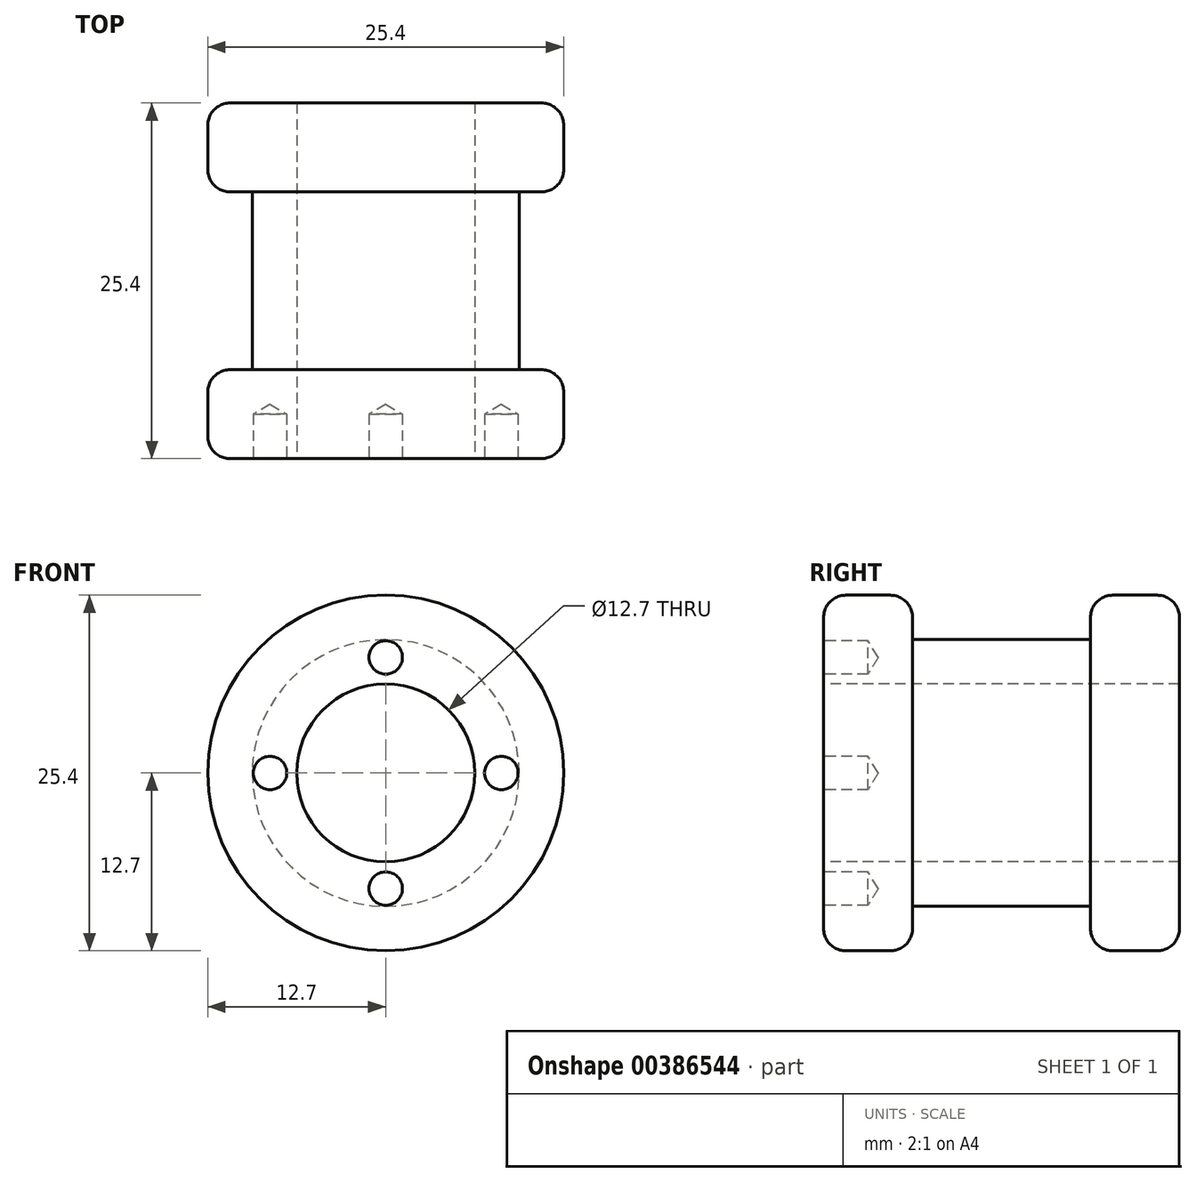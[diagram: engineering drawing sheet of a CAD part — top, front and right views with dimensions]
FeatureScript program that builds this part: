
annotation { "Feature Type Name" : "Feature", "Feature Type Description" : "" }
export const myFeature = defineFeature(function(context is Context, id is Id, definition is map)
    precondition{}
    {
        {
            var Q0;
            Q0=qCreatedBy(makeId("Front.planeOp"),FACE);
            var sketch = newSketch(context, id + "F0", { "sketchPlane" : qUnion([Q0])});
            skCircle(sketch, "E0", {"center": v(0, 0) * mm, "radius": 12.7 * mm});
            skSolve(sketch);
        }
        {
            var Q0;
            Q0 = qSketchRegion(id + "F0", true);
            extrude(context, id + "F1", {"entities" : qUnion([Q0]), "depth" : 6.35 * mm});
        }
        {
            var Q0;
            Q0=makeQuery(id+"F1.opExtrude","CAP_FACE",FACE,{"disambiguationData":[OSD([sQuery(id+"F0.wireOp",EDGE,"E0")])],"isStart":false});
            var sketch = newSketch(context, id + "F2", { "sketchPlane" : qUnion([Q0])});
            skCircle(sketch, "E1", {"center": v(0, 0) * mm, "radius": 9.52 * mm});
            skSolve(sketch);
        }
        {
            var Q0;
            Q0 = qSketchRegion(id + "F2", true);
            extrude(context, id + "F3", {"entities" : qUnion([Q0]), "operationType" : NewBodyOperationType.ADD, "depth" : 12.7 * mm});
        }
        {
            var Q0;
            Q0=makeQuery(id+"F3.opExtrude","CAP_FACE",FACE,{"disambiguationData":[OSD([sQuery(id+"F2.wireOp",EDGE,"E1")])],"isStart":false});
            var sketch = newSketch(context, id + "F4", { "sketchPlane" : qUnion([Q0])});
            skCircle(sketch, "E2", {"center": v(0, 0) * mm, "radius": 12.7 * mm});
            skSolve(sketch);
        }
        {
            var Q0;
            Q0 = qSketchRegion(id + "F4", true);
            extrude(context, id + "F5", {"entities" : qUnion([Q0]), "operationType" : NewBodyOperationType.ADD, "depth" : 6.35 * mm});
        }
        {
            var Q0;
            Q0=makeQuery(id+"F1.opExtrude","CAP_EDGE",EDGE,{"disambiguationData":[OSD([sQuery(id+"F0.wireOp",EDGE,"E0")])],"isStart":true});
            var Q1;
            Q1=makeQuery(id+"F1.opExtrude","CAP_EDGE",EDGE,{"disambiguationData":[OSD([sQuery(id+"F0.wireOp",EDGE,"E0")])],"isStart":false});
            var Q2;
            Q2=makeQuery(id+"F5.opExtrude","SWEPT_FACE",FACE,{"disambiguationData":[OSD([sQuery(id+"F4.wireOp",EDGE,"E2")])]});
            var Q3;
            Q3=makeQuery(id+"F3.opExtrude","CAP_EDGE",EDGE,{"disambiguationData":[OSD([sQuery(id+"F2.wireOp",EDGE,"E1")])],"isStart":true});
            var Q4;
            Q4=makeQuery(id+"F3.opExtrude","CAP_EDGE",EDGE,{"disambiguationData":[OSD([sQuery(id+"F2.wireOp",EDGE,"E1")])],"isStart":false});
            fillet(context, id + "F6", {"entities" : qUnion([Q0, Q1, Q2, Q3, Q4]), "radius" : 1.59 * mm, "tangentPropagation" : true, "allowEdgeOverflow" : false});
        }
        {
            var Q0;
            Q0=makeQuery(id+"F5.opExtrude","CAP_FACE",FACE,{"disambiguationData":[OSD([sQuery(id+"F4.wireOp",EDGE,"E2")])],"isStart":false});
            var sketch = newSketch(context, id + "F7", { "sketchPlane" : qUnion([Q0])});
            skPoint(sketch, "E3", {"position": v(0, 0) * mm});
            skPoint(sketch, "E4", {"position": v(0, 8.26) * mm});
            skPoint(sketch, "E5", {"position": v(8.26, 0) * mm});
            skPoint(sketch, "E6", {"position": v(-8.26, 0) * mm});
            skPoint(sketch, "E7", {"position": v(0, -8.26) * mm});
            skSolve(sketch);
        }
        {
            var Q0;
            Q0=sQuery(id+"F7.wireOp",VERTEX,"E3");
            var Q1;
            Q1=makeQuery(id+"F1.opExtrude","SWEPT_BODY",BODY,{"disambiguationData":[OSD([sQuery(id+"F0.wireOp",EDGE,"E0")])]});
            hole(context, id + "F8", {"style" : HoleStyle.SIMPLE, "endStyle" : HoleEndStyle.THROUGH, "holeDiameter" : 12.7 * mm, "isTappedThrough" : true, "tappedDepth" : 12.7 * mm, "tapClearance" : 3, "startFromSketch" : true, "locations" : qUnion([Q0]), "scope" : qUnion([Q1])});
        }
        {
            var Q0;
            Q0=sQuery(id+"F7.wireOp",VERTEX,"E4");
            var Q1;
            Q1=sQuery(id+"F7.wireOp",VERTEX,"E5");
            var Q2;
            Q2=sQuery(id+"F7.wireOp",VERTEX,"E7");
            var Q3;
            Q3=sQuery(id+"F7.wireOp",VERTEX,"E6");
            var Q4;
            Q4=makeQuery(id+"F1.opExtrude","SWEPT_BODY",BODY,{"disambiguationData":[OSD([sQuery(id+"F0.wireOp",EDGE,"E0")])]});
            hole(context, id + "F9", {"style" : HoleStyle.SIMPLE, "endStyle" : HoleEndStyle.BLIND, "holeDiameter" : 2.4 * mm, "holeDepth" : 3.17 * mm, "isTappedThrough" : true, "tappedDepth" : 12.7 * mm, "tapClearance" : 3, "startFromSketch" : true, "locations" : qUnion([Q0, Q1, Q2, Q3]), "scope" : qUnion([Q4])});
        }
    });
